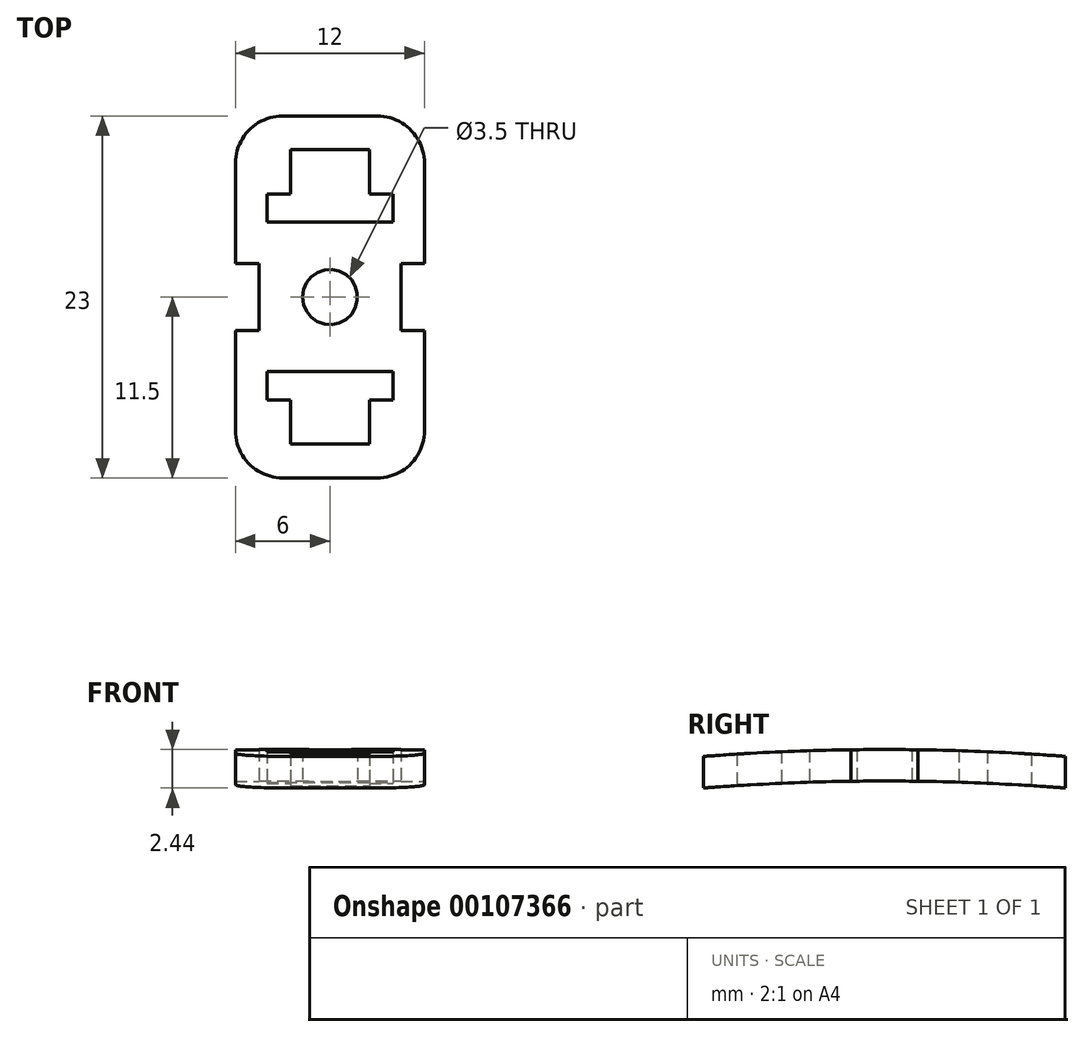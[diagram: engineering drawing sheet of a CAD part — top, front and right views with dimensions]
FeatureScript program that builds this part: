
annotation { "Feature Type Name" : "Feature", "Feature Type Description" : "" }
export const myFeature = defineFeature(function(context is Context, id is Id, definition is map)
    precondition{}
    {
        {
            var Q0;
            Q0=qCreatedBy(makeId("Top.planeOp"),FACE);
            var sketch = newSketch(context, id + "F0", { "sketchPlane" : qUnion([Q0])});
            skLineSegment(sketch, "E0", {"start": v(-4.5, 0) * mm, "end": v(-4.5, 2.12) * mm});
            skLineSegment(sketch, "E1", {"start": v(-4.5, 2.12) * mm, "end": v(-6, 2.12) * mm});
            skLineSegment(sketch, "E2", {"start": v(-6, 2.12) * mm, "end": v(-6, 8.5) * mm});
            skLineSegment(sketch, "E3", {"start": v(-3, 11.5) * mm, "end": v(0, 11.5) * mm});
            skPoint(sketch, "E4.visualSharp", {"position": v(-6, 11.5) * mm});
            skArc(sketch, "E4.filletArc", {"start": v(-3, 11.5) * mm, "mid": v(-5.12, 10.62) * mm, "end": v(-6, 8.5) * mm});
            skLineSegment(sketch, "E5.MirrorCS", {"start": v(3, 11.5) * mm, "end": v(0, 11.5) * mm});
            skArc(sketch, "E6.MirrorCS", {"start": v(3, 11.5) * mm, "mid": v(5.12, 10.62) * mm, "end": v(6, 8.5) * mm});
            skLineSegment(sketch, "E7.MirrorCS", {"start": v(6, 2.12) * mm, "end": v(6, 8.5) * mm});
            skLineSegment(sketch, "E8.MirrorCS", {"start": v(4.5, 2.12) * mm, "end": v(6, 2.12) * mm});
            skLineSegment(sketch, "E9.MirrorCS", {"start": v(4.5, 0) * mm, "end": v(4.5, 2.12) * mm});
            skLineSegment(sketch, "E10.MirrorCS", {"start": v(-4.5, 0) * mm, "end": v(-4.5, -2.12) * mm});
            skLineSegment(sketch, "E11.MirrorCS", {"start": v(-4.5, -2.12) * mm, "end": v(-6, -2.12) * mm});
            skLineSegment(sketch, "E12.MirrorCS", {"start": v(-6, -2.12) * mm, "end": v(-6, -8.5) * mm});
            skArc(sketch, "E13.MirrorCS", {"start": v(-3, -11.5) * mm, "mid": v(-5.12, -10.62) * mm, "end": v(-6, -8.5) * mm});
            skLineSegment(sketch, "E14.MirrorCS", {"start": v(-3, -11.5) * mm, "end": v(0, -11.5) * mm});
            skLineSegment(sketch, "E15.MirrorCS", {"start": v(3, -11.5) * mm, "end": v(0, -11.5) * mm});
            skArc(sketch, "E16.MirrorCS", {"start": v(3, -11.5) * mm, "mid": v(5.12, -10.62) * mm, "end": v(6, -8.5) * mm});
            skLineSegment(sketch, "E17.MirrorCS", {"start": v(6, -2.12) * mm, "end": v(6, -8.5) * mm});
            skLineSegment(sketch, "E18.MirrorCS", {"start": v(4.5, -2.12) * mm, "end": v(6, -2.12) * mm});
            skLineSegment(sketch, "E19.MirrorCS", {"start": v(4.5, 0) * mm, "end": v(4.5, -2.12) * mm});
            skLineSegment(sketch, "E20", {"start": v(-4, 4.75) * mm, "end": v(0, 4.75) * mm});
            skLineSegment(sketch, "E21", {"start": v(-4, 4.75) * mm, "end": v(-4, 6.55) * mm});
            skLineSegment(sketch, "E22", {"start": v(-4, 6.55) * mm, "end": v(-2.5, 6.55) * mm});
            skLineSegment(sketch, "E23", {"start": v(-2.5, 6.55) * mm, "end": v(-2.5, 9.35) * mm});
            skLineSegment(sketch, "E24", {"start": v(-2.5, 9.35) * mm, "end": v(0, 9.35) * mm});
            skLineSegment(sketch, "E25.MirrorCS", {"start": v(2.5, 9.35) * mm, "end": v(0, 9.35) * mm});
            skLineSegment(sketch, "E26.MirrorCS", {"start": v(2.5, 6.55) * mm, "end": v(2.5, 9.35) * mm});
            skLineSegment(sketch, "E27.MirrorCS", {"start": v(4, 6.55) * mm, "end": v(2.5, 6.55) * mm});
            skLineSegment(sketch, "E28.MirrorCS", {"start": v(4, 4.75) * mm, "end": v(4, 6.55) * mm});
            skLineSegment(sketch, "E29.MirrorCS", {"start": v(4, 4.75) * mm, "end": v(0, 4.75) * mm});
            skLineSegment(sketch, "E30.MirrorCS", {"start": v(4, -4.75) * mm, "end": v(0, -4.75) * mm});
            skLineSegment(sketch, "E31.MirrorCS", {"start": v(4, -4.75) * mm, "end": v(4, -6.55) * mm});
            skLineSegment(sketch, "E32.MirrorCS", {"start": v(4, -6.55) * mm, "end": v(2.5, -6.55) * mm});
            skLineSegment(sketch, "E33.MirrorCS", {"start": v(2.5, -6.55) * mm, "end": v(2.5, -9.35) * mm});
            skLineSegment(sketch, "E34.MirrorCS", {"start": v(2.5, -9.35) * mm, "end": v(0, -9.35) * mm});
            skLineSegment(sketch, "E35.MirrorCS", {"start": v(-2.5, -9.35) * mm, "end": v(0, -9.35) * mm});
            skLineSegment(sketch, "E36.MirrorCS", {"start": v(-2.5, -6.55) * mm, "end": v(-2.5, -9.35) * mm});
            skLineSegment(sketch, "E37.MirrorCS", {"start": v(-4, -6.55) * mm, "end": v(-2.5, -6.55) * mm});
            skLineSegment(sketch, "E38.MirrorCS", {"start": v(-4, -4.75) * mm, "end": v(-4, -6.55) * mm});
            skLineSegment(sketch, "E39.MirrorCS", {"start": v(-4, -4.75) * mm, "end": v(0, -4.75) * mm});
            skCircle(sketch, "E40", {"center": v(0, 0) * mm, "radius": 1.75 * mm});
            skSolve(sketch);
        }
        {
            var Q0;
            Q0=makeQuery(id+"F0.imprint","IMPRINT",FACE,{"disambiguationData":[TD([[makeQuery(id+"F0.imprint","IMPRINT",EDGE,{"derivedFrom":sQuery(id+"F0.wireOp",EDGE,"E0")}),-1.0]])]});
            extrude(context, id + "F1", {"entities" : qUnion([Q0]), "depth" : 5 * mm, "hasSecondDirection" : true, "secondDirectionOppositeDirection" : true, "secondDirectionDepth" : 5 * mm});
        }
        {
            var Q0;
            Q0=qCreatedBy(makeId("Right.planeOp"),FACE);
            var sketch = newSketch(context, id + "F2", { "sketchPlane" : qUnion([Q0])});
            skArc(sketch, "E41", {"start": v(38.82, -5.11) * mm, "mid": v(0, 0) * mm, "end": v(-38.82, -5.11) * mm});
            skLineSegment(sketch, "E42", {"start": v(38.82, -5.11) * mm, "end": v(0, -150) * mm});
            skLineSegment(sketch, "E43", {"start": v(-38.82, -5.11) * mm, "end": v(0, -150) * mm});
            skArc(sketch, "E44", {"start": v(39.34, -3.18) * mm, "mid": v(0, 2) * mm, "end": v(-39.34, -3.18) * mm});
            skLineSegment(sketch, "E45", {"start": v(39.34, 12) * mm, "end": v(-39.34, 12) * mm});
            skLineSegment(sketch, "E46", {"start": v(-39.34, 12) * mm, "end": v(-39.34, -3.18) * mm});
            skLineSegment(sketch, "E47", {"start": v(39.34, 12) * mm, "end": v(39.34, -3.18) * mm});
            skLineSegment(sketch, "E48", {"start": v(38.82, -5.11) * mm, "end": v(39.34, -3.18) * mm, "construction": true});
            skLineSegment(sketch, "E49", {"start": v(-38.82, -5.11) * mm, "end": v(-39.34, -3.18) * mm, "construction": true});
            skSolve(sketch);
        }
        {
            var Q0;
            Q0=makeQuery(id+"F2.imprint","IMPRINT",FACE,{"disambiguationData":[TD([[makeQuery(id+"F2.imprint","IMPRINT",EDGE,{"derivedFrom":sQuery(id+"F2.wireOp",EDGE,"E44")}),-1.0]])]});
            var Q1;
            Q1=makeQuery(id+"F2.imprint","IMPRINT",FACE,{"disambiguationData":[TD([[makeQuery(id+"F2.imprint","IMPRINT",EDGE,{"derivedFrom":sQuery(id+"F2.wireOp",EDGE,"E41")}),1.0]])]});
            extrude(context, id + "F3", {"entities" : qUnion([Q0, Q1]), "operationType" : NewBodyOperationType.REMOVE, "oppositeDirection" : true, "depth" : 10 * mm, "hasSecondDirection" : true, "secondDirectionOppositeDirection" : false, "secondDirectionDepth" : 10 * mm});
        }
    });
